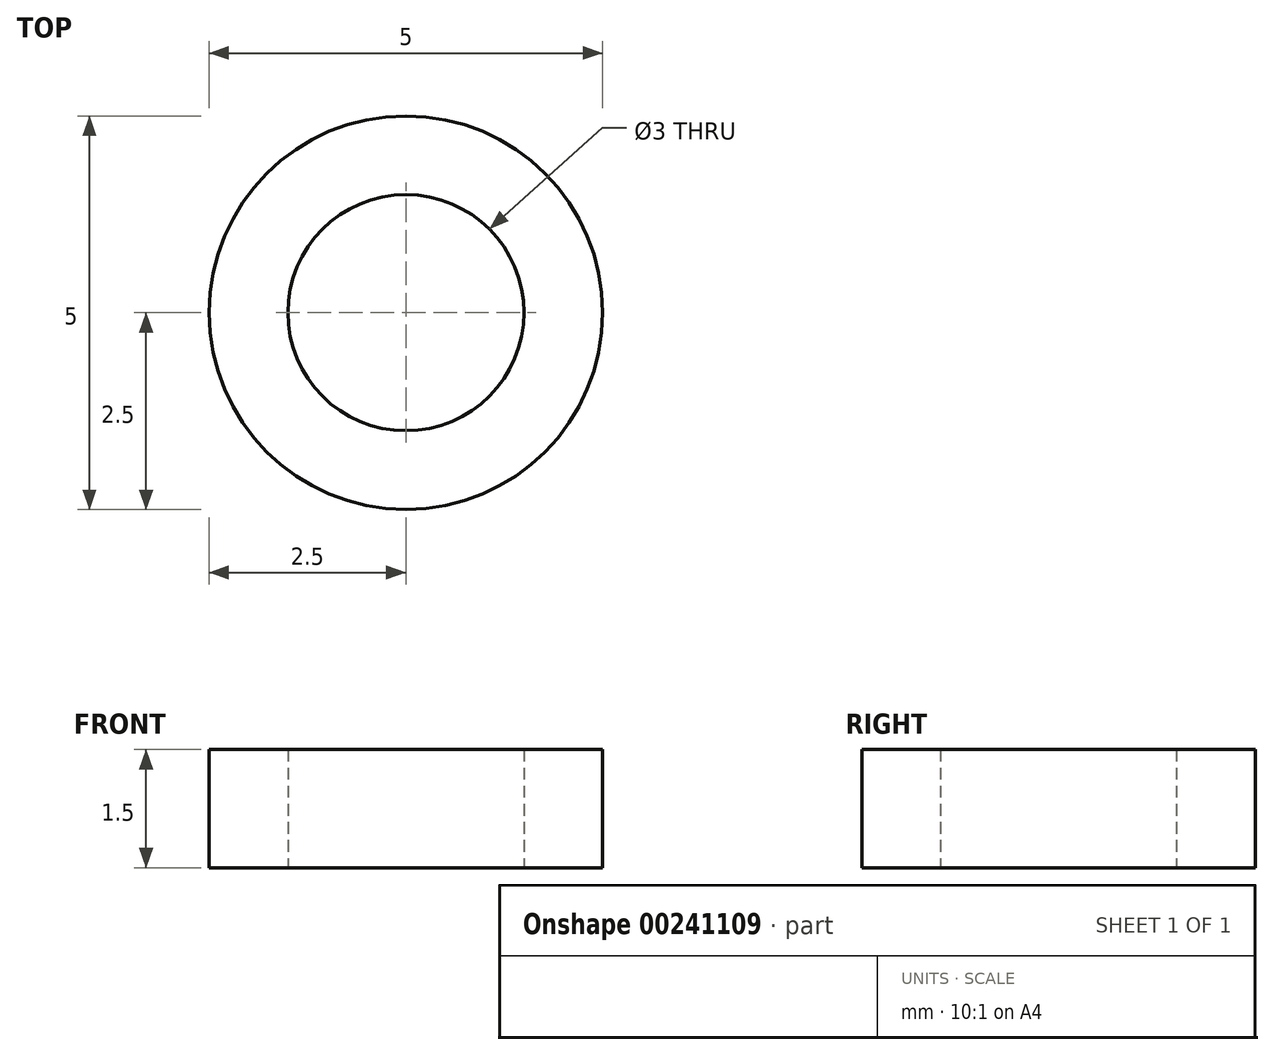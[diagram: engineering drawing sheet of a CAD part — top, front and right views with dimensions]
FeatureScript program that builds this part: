
annotation { "Feature Type Name" : "Feature", "Feature Type Description" : "" }
export const myFeature = defineFeature(function(context is Context, id is Id, definition is map)
    precondition{}
    {
        {
            var Q0;
            Q0=qCreatedBy(makeId("Top.planeOp"),FACE);
            var sketch = newSketch(context, id + "F0", { "sketchPlane" : qUnion([Q0])});
            skCircle(sketch, "E0", {"center": v(0, 0) * mm, "radius": 1.5 * mm});
            skCircle(sketch, "E1", {"center": v(0, 0) * mm, "radius": 2.5 * mm});
            skSolve(sketch);
        }
        {
            var Q0;
            Q0 = qSketchRegion(id + "F0", true);
            extrude(context, id + "F1", {"entities" : qUnion([Q0]), "depth" : 1.5 * mm});
        }
    });
